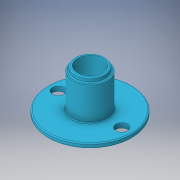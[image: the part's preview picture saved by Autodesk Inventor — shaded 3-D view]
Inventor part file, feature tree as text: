
AUTODESK INVENTOR PART (.ipt)
format: ipt  version: 2016 (Build 200138000, 138)  size: 175,104 bytes
history: native  units: in
note: dims shown in document units (in); Inventor stores cm internally (conversion verified against a paired STEP export)
features: extrude x4, sketch x4, fillet x1
ambient origin geometry x8: Origin, YZ Plane, XZ Plane, XY Plane, X Axis, Y Axis, Z Axis, Center Point
bodies: Solid1 (feature_tree)
feature tree (9):
  extrude  "Extrusion1"  Depth=0.243in
  extrude  "Extrusion3"  Depth=0.045in
  extrude  "Extrusion2"  Depth=0.3065in
  extrude  "Extrusion4"  Depth=0.01in TaperAngle=360.0deg
  fillet  "Fillet1"  Radius=0.365in
  sketch  "Sketch1"  dims[d0=0.808in d1=0.243in]
  sketch  "Sketch2"  dims[d2=0.045in d3=0.0in d4=0.333in]
  sketch  "Sketch3"  dims[d5=0.365in d6=0.0in d7=0.3065in]
  sketch  "Sketch4"  dims[d8=0.114in d9=0.7874in d11=360.0deg d13=0.365in d14=0.0in d15=0.289in d16=0.045in d17=0.0in d18=0.01in]
